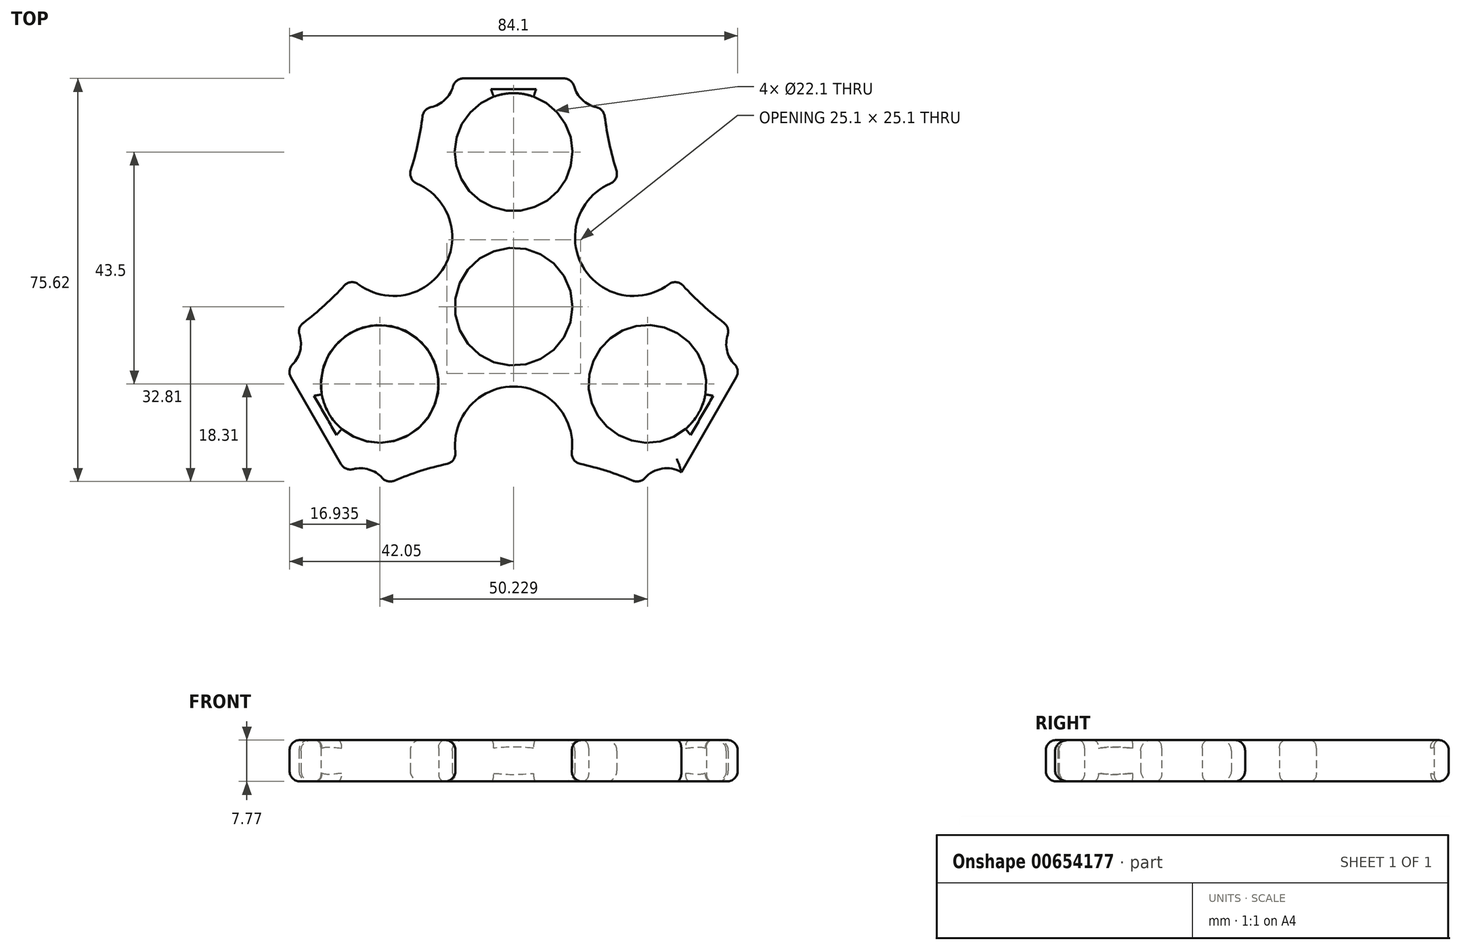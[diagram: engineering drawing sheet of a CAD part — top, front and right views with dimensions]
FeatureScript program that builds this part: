
annotation { "Feature Type Name" : "Feature", "Feature Type Description" : "" }
export const myFeature = defineFeature(function(context is Context, id is Id, definition is map)
    precondition{}
    {
        {
            var Q0;
            Q0=qCreatedBy(makeId("Top.planeOp"),FACE);
            var sketch = newSketch(context, id + "F0", { "sketchPlane" : qUnion([Q0])});
            skLineSegment(sketch, "E0", {"start": v(0, 0) * mm, "end": v(-25.11, -14.5) * mm});
            skLineSegment(sketch, "E1", {"start": v(-25.11, -14.5) * mm, "end": v(0, 0) * mm});
            skLineSegment(sketch, "E2", {"start": v(0, 0) * mm, "end": v(0, 29) * mm});
            skLineSegment(sketch, "E3", {"start": v(0, 29) * mm, "end": v(0, 0) * mm});
            skLineSegment(sketch, "E4", {"start": v(0, 0) * mm, "end": v(25.11, -14.5) * mm});
            skLineSegment(sketch, "E5", {"start": v(25.11, -14.5) * mm, "end": v(0, 0) * mm});
            skCircle(sketch, "E6", {"center": v(0, 29) * mm, "radius": 11.05 * mm});
            skCircle(sketch, "E7", {"center": v(-25.11, -14.5) * mm, "radius": 11.05 * mm});
            skCircle(sketch, "E8", {"center": v(25.11, -14.5) * mm, "radius": 11.05 * mm});
            skCircle(sketch, "E9", {"center": v(0, 0) * mm, "radius": 11.05 * mm});
            skCircle(sketch, "E10", {"center": v(-25.11, -14.5) * mm, "radius": 12.5 * mm});
            skCircle(sketch, "E11", {"center": v(0, 29) * mm, "radius": 12.5 * mm});
            skCircle(sketch, "E12", {"center": v(25.11, -14.5) * mm, "radius": 12.5 * mm});
            skLineSegment(sketch, "E13.0", {"start": v(74.15, 42.8) * mm, "end": v(0, -85.62) * mm});
            skLineSegment(sketch, "E13.1", {"start": v(0, -85.62) * mm, "end": v(-74.15, 42.8) * mm});
            skLineSegment(sketch, "E13.2", {"start": v(-74.15, 42.8) * mm, "end": v(74.15, 42.8) * mm});
            skPoint(sketch, "E13.0.midPoint", {"position": v(37.07, -21.4) * mm});
            skCircle(sketch, "E14", {"center": v(-74.15, 42.8) * mm, "radius": 57.5 * mm});
            skCircle(sketch, "E15", {"center": v(74.15, 42.8) * mm, "radius": 57.5 * mm});
            skCircle(sketch, "E16", {"center": v(0, -85.62) * mm, "radius": 57.5 * mm});
            skCircle(sketch, "E17", {"center": v(16.65, 42.8) * mm, "radius": 5.5 * mm});
            skCircle(sketch, "E18", {"center": v(-16.65, 42.8) * mm, "radius": 5.5 * mm});
            skCircle(sketch, "E19", {"center": v(-45.4, -6.99) * mm, "radius": 5.5 * mm});
            skCircle(sketch, "E20", {"center": v(-28.75, -35.82) * mm, "radius": 5.5 * mm});
            skCircle(sketch, "E21", {"center": v(28.75, -35.82) * mm, "radius": 5.5 * mm});
            skCircle(sketch, "E22", {"center": v(45.4, -6.99) * mm, "radius": 5.5 * mm});
            skLineSegment(sketch, "E23", {"start": v(25.11, -14.5) * mm, "end": v(-24.35, 14.06) * mm});
            skLineSegment(sketch, "E24", {"start": v(-25.11, -14.5) * mm, "end": v(24.35, 14.06) * mm});
            skLineSegment(sketch, "E25", {"start": v(0, 29) * mm, "end": v(0, -28.12) * mm});
            skCircle(sketch, "E26", {"center": v(22.52, 13) * mm, "radius": 11 * mm});
            skCircle(sketch, "E27", {"center": v(0, -26) * mm, "radius": 11 * mm});
            skCircle(sketch, "E28", {"center": v(-22.52, 13) * mm, "radius": 11 * mm});
            skSolve(sketch);
        }
        {
            var Q0;
            Q0=makeQuery(id+"F0.imprint","IMPRINT",FACE,{"disambiguationData":[TD([[makeQuery(id+"F0.imprint","IMPRINT",EDGE,{"derivedFrom":sQuery(id+"F0.wireOp",EDGE,"E11")}),-1.0]])]});
            var Q1;
            Q1=makeQuery(id+"F0.imprint","IMPRINT",FACE,{"disambiguationData":[TD([[makeQuery(id+"F0.imprint","IMPRINT",EDGE,{"derivedFrom":sQuery(id+"F0.wireOp",EDGE,"E10")}),-1.0]])]});
            var Q2;
            Q2=makeQuery(id+"F0.imprint","IMPRINT",FACE,{"disambiguationData":[TD([[makeQuery(id+"F0.imprint","IMPRINT",EDGE,{"derivedFrom":sQuery(id+"F0.wireOp",EDGE,"E12")}),-1.0]])]});
            var Q3;
            Q3=makeQuery(id+"F0.imprint","IMPRINT",FACE,{"disambiguationData":[TD([[makeQuery(id+"F0.imprint","IMPRINT",EDGE,{"derivedFrom":sQuery(id+"F0.wireOp",EDGE,"E6")}),-1.0]])]});
            var Q4;
            Q4=makeQuery(id+"F0.imprint","IMPRINT",FACE,{"disambiguationData":[TD([[makeQuery(id+"F0.imprint","IMPRINT",EDGE,{"derivedFrom":sQuery(id+"F0.wireOp",EDGE,"E7")}),-1.0]])]});
            var Q5;
            Q5=makeQuery(id+"F0.imprint","IMPRINT",FACE,{"disambiguationData":[TD([[makeQuery(id+"F0.imprint","IMPRINT",EDGE,{"derivedFrom":sQuery(id+"F0.wireOp",EDGE,"E8")}),-1.0]])]});
            extrude(context, id + "F1", {"entities" : qUnion([Q0, Q1, Q2, Q3, Q4, Q5]), "depth" : 7.77 * mm, "offsetDistance" : 25 * mm});
        }
        {
            var Q0;
            Q0=makeQuery(id+"F1.opExtrude","CAP_EDGE",EDGE,{"disambiguationData":[OSD([sQuery(id+"F0.wireOp",EDGE,"E13.2")])],"isStart":false});
            var Q1;
            Q1=makeQuery(id+"F1.opExtrude","CAP_EDGE",EDGE,{"disambiguationData":[OSD([sQuery(id+"F0.wireOp",EDGE,"E18")])],"isStart":true});
            var Q2;
            {var subQ0=sQuery(id+"F0.wireOp",EDGE,"E14");Q2=makeQuery(id+"F1.opExtrude","CAP_EDGE",EDGE,{"disambiguationData":[OSD([subQ0]),TDD([makeQuery(id+"F0.imprint","IMPRINT",EDGE,{"disambiguationData":[TD([[makeQuery(id+"F0.imprint","INTERSECT",VERTEX,{"disambiguationData":[OD(1.0)],"derivedFrom":[subQ0,sQuery(id+"F0.wireOp",EDGE,"tso12NrA-vn6K-p382-kDVD-uUXhCmWPkcJA")]}),-1.0]])],"derivedFrom":subQ0})])],"isStart":false});}
            var Q3;
            Q3=makeQuery(id+"F1.opExtrude","CAP_EDGE",EDGE,{"disambiguationData":[OSD([sQuery(id+"F0.wireOp",EDGE,"E18")])],"isStart":false});
            var Q4;
            Q4=makeQuery(id+"F1.opExtrude","CAP_EDGE",EDGE,{"disambiguationData":[OSD([sQuery(id+"F0.wireOp",EDGE,"tso12NrA-vn6K-p382-kDVD-uUXhCmWPkcJA")])],"isStart":false});
            var Q5;
            {var subQ0=sQuery(id+"F0.wireOp",EDGE,"E14");Q5=makeQuery(id+"F1.opExtrude","CAP_EDGE",EDGE,{"disambiguationData":[OSD([subQ0]),TDD([makeQuery(id+"F0.imprint","IMPRINT",EDGE,{"disambiguationData":[TD([[makeQuery(id+"F0.imprint","INTERSECT",VERTEX,{"disambiguationData":[OD(1.0)],"derivedFrom":[subQ0,sQuery(id+"F0.wireOp",EDGE,"E19")]}),-1.0]])],"derivedFrom":subQ0})])],"isStart":false});}
            var Q6;
            Q6=makeQuery(id+"F1.opExtrude","CAP_EDGE",EDGE,{"disambiguationData":[OSD([sQuery(id+"F0.wireOp",EDGE,"E19")])],"isStart":false});
            var Q7;
            Q7=makeQuery(id+"F1.opExtrude","CAP_EDGE",EDGE,{"disambiguationData":[OSD([sQuery(id+"F0.wireOp",EDGE,"E13.1")])],"isStart":false});
            var Q8;
            Q8=makeQuery(id+"F1.opExtrude","CAP_EDGE",EDGE,{"disambiguationData":[OSD([sQuery(id+"F0.wireOp",EDGE,"E20")])],"isStart":false});
            var Q9;
            {var subQ0=sQuery(id+"F0.wireOp",EDGE,"E16");Q9=makeQuery(id+"F1.opExtrude","CAP_EDGE",EDGE,{"disambiguationData":[OSD([subQ0]),TDD([makeQuery(id+"F0.imprint","IMPRINT",EDGE,{"disambiguationData":[TD([[makeQuery(id+"F0.imprint","INTERSECT",VERTEX,{"disambiguationData":[OD(1.0)],"derivedFrom":[subQ0,sQuery(id+"F0.wireOp",EDGE,"W5DYfLWn-jYW6-ROIx-5Qjh-cELPhGJE8ypl")]}),-1.0]])],"derivedFrom":subQ0})])],"isStart":false});}
            var Q10;
            Q10=makeQuery(id+"F1.opExtrude","CAP_EDGE",EDGE,{"disambiguationData":[OSD([sQuery(id+"F0.wireOp",EDGE,"W5DYfLWn-jYW6-ROIx-5Qjh-cELPhGJE8ypl")])],"isStart":false});
            var Q11;
            {var subQ0=sQuery(id+"F0.wireOp",EDGE,"E16");Q11=makeQuery(id+"F1.opExtrude","CAP_EDGE",EDGE,{"disambiguationData":[OSD([subQ0]),TDD([makeQuery(id+"F0.imprint","IMPRINT",EDGE,{"disambiguationData":[TD([[makeQuery(id+"F0.imprint","INTERSECT",VERTEX,{"disambiguationData":[OD(1.0)],"derivedFrom":[subQ0,sQuery(id+"F0.wireOp",EDGE,"E21")]}),-1.0]])],"derivedFrom":subQ0})])],"isStart":false});}
            var Q12;
            Q12=makeQuery(id+"F1.opExtrude","CAP_EDGE",EDGE,{"disambiguationData":[OSD([sQuery(id+"F0.wireOp",EDGE,"E21")])],"isStart":false});
            var Q13;
            Q13=makeQuery(id+"F1.opExtrude","CAP_EDGE",EDGE,{"disambiguationData":[OSD([sQuery(id+"F0.wireOp",EDGE,"E13.0")])],"isStart":false});
            var Q14;
            Q14=makeQuery(id+"F1.opExtrude","CAP_EDGE",EDGE,{"disambiguationData":[OSD([sQuery(id+"F0.wireOp",EDGE,"E22")])],"isStart":false});
            var Q15;
            {var subQ0=sQuery(id+"F0.wireOp",EDGE,"E15");Q15=makeQuery(id+"F1.opExtrude","CAP_EDGE",EDGE,{"disambiguationData":[OSD([subQ0]),TDD([makeQuery(id+"F0.imprint","IMPRINT",EDGE,{"disambiguationData":[TD([[makeQuery(id+"F0.imprint","INTERSECT",VERTEX,{"disambiguationData":[OD(1.0)],"derivedFrom":[subQ0,sQuery(id+"F0.wireOp",EDGE,"gOxveVNV-1YZB-HPbS-OaDW-XKyIJjo2ujh9")]}),-1.0]])],"derivedFrom":subQ0})])],"isStart":false});}
            var Q16;
            Q16=makeQuery(id+"F1.opExtrude","CAP_EDGE",EDGE,{"disambiguationData":[OSD([sQuery(id+"F0.wireOp",EDGE,"gOxveVNV-1YZB-HPbS-OaDW-XKyIJjo2ujh9")])],"isStart":false});
            var Q17;
            {var subQ0=sQuery(id+"F0.wireOp",EDGE,"E15");Q17=makeQuery(id+"F1.opExtrude","CAP_EDGE",EDGE,{"disambiguationData":[OSD([subQ0]),TDD([makeQuery(id+"F0.imprint","IMPRINT",EDGE,{"disambiguationData":[TD([[makeQuery(id+"F0.imprint","INTERSECT",VERTEX,{"disambiguationData":[OD(1.0)],"derivedFrom":[subQ0,sQuery(id+"F0.wireOp",EDGE,"E17")]}),-1.0]])],"derivedFrom":subQ0})])],"isStart":false});}
            var Q18;
            Q18=makeQuery(id+"F1.opExtrude","CAP_EDGE",EDGE,{"disambiguationData":[OSD([sQuery(id+"F0.wireOp",EDGE,"E17")])],"isStart":false});
            var Q19;
            Q19=makeQuery(id+"F1.opExtrude","CAP_EDGE",EDGE,{"disambiguationData":[OSD([sQuery(id+"F0.wireOp",EDGE,"E13.2")])],"isStart":true});
            var Q20;
            Q20=makeQuery(id+"F1.opExtrude","CAP_EDGE",EDGE,{"disambiguationData":[OSD([sQuery(id+"F0.wireOp",EDGE,"E17")])],"isStart":true});
            var Q21;
            {var subQ0=sQuery(id+"F0.wireOp",EDGE,"E15");Q21=makeQuery(id+"F1.opExtrude","CAP_EDGE",EDGE,{"disambiguationData":[OSD([subQ0]),TDD([makeQuery(id+"F0.imprint","IMPRINT",EDGE,{"disambiguationData":[TD([[makeQuery(id+"F0.imprint","INTERSECT",VERTEX,{"disambiguationData":[OD(1.0)],"derivedFrom":[subQ0,sQuery(id+"F0.wireOp",EDGE,"E17")]}),-1.0]])],"derivedFrom":subQ0})])],"isStart":true});}
            var Q22;
            Q22=makeQuery(id+"F1.opExtrude","CAP_EDGE",EDGE,{"disambiguationData":[OSD([sQuery(id+"F0.wireOp",EDGE,"gOxveVNV-1YZB-HPbS-OaDW-XKyIJjo2ujh9")])],"isStart":true});
            var Q23;
            {var subQ0=sQuery(id+"F0.wireOp",EDGE,"E14");Q23=makeQuery(id+"F1.opExtrude","CAP_EDGE",EDGE,{"disambiguationData":[OSD([subQ0]),TDD([makeQuery(id+"F0.imprint","IMPRINT",EDGE,{"disambiguationData":[TD([[makeQuery(id+"F0.imprint","INTERSECT",VERTEX,{"disambiguationData":[OD(1.0)],"derivedFrom":[subQ0,sQuery(id+"F0.wireOp",EDGE,"tso12NrA-vn6K-p382-kDVD-uUXhCmWPkcJA")]}),-1.0]])],"derivedFrom":subQ0})])],"isStart":true});}
            var Q24;
            Q24=makeQuery(id+"F1.opExtrude","CAP_EDGE",EDGE,{"disambiguationData":[OSD([sQuery(id+"F0.wireOp",EDGE,"tso12NrA-vn6K-p382-kDVD-uUXhCmWPkcJA")])],"isStart":true});
            var Q25;
            {var subQ0=sQuery(id+"F0.wireOp",EDGE,"E15");Q25=makeQuery(id+"F1.opExtrude","CAP_EDGE",EDGE,{"disambiguationData":[OSD([subQ0]),TDD([makeQuery(id+"F0.imprint","IMPRINT",EDGE,{"disambiguationData":[TD([[makeQuery(id+"F0.imprint","INTERSECT",VERTEX,{"disambiguationData":[OD(1.0)],"derivedFrom":[subQ0,sQuery(id+"F0.wireOp",EDGE,"gOxveVNV-1YZB-HPbS-OaDW-XKyIJjo2ujh9")]}),-1.0]])],"derivedFrom":subQ0})])],"isStart":true});}
            var Q26;
            Q26=makeQuery(id+"F1.opExtrude","CAP_EDGE",EDGE,{"disambiguationData":[OSD([sQuery(id+"F0.wireOp",EDGE,"E22")])],"isStart":true});
            var Q27;
            Q27=makeQuery(id+"F1.opExtrude","CAP_EDGE",EDGE,{"disambiguationData":[OSD([sQuery(id+"F0.wireOp",EDGE,"E13.0")])],"isStart":true});
            var Q28;
            Q28=makeQuery(id+"F1.opExtrude","CAP_EDGE",EDGE,{"disambiguationData":[OSD([sQuery(id+"F0.wireOp",EDGE,"E21")])],"isStart":true});
            var Q29;
            {var subQ0=sQuery(id+"F0.wireOp",EDGE,"E16");Q29=makeQuery(id+"F1.opExtrude","CAP_EDGE",EDGE,{"disambiguationData":[OSD([subQ0]),TDD([makeQuery(id+"F0.imprint","IMPRINT",EDGE,{"disambiguationData":[TD([[makeQuery(id+"F0.imprint","INTERSECT",VERTEX,{"disambiguationData":[OD(1.0)],"derivedFrom":[subQ0,sQuery(id+"F0.wireOp",EDGE,"E21")]}),-1.0]])],"derivedFrom":subQ0})])],"isStart":true});}
            var Q30;
            Q30=makeQuery(id+"F1.opExtrude","CAP_EDGE",EDGE,{"disambiguationData":[OSD([sQuery(id+"F0.wireOp",EDGE,"W5DYfLWn-jYW6-ROIx-5Qjh-cELPhGJE8ypl")])],"isStart":true});
            var Q31;
            {var subQ0=sQuery(id+"F0.wireOp",EDGE,"E16");Q31=makeQuery(id+"F1.opExtrude","CAP_EDGE",EDGE,{"disambiguationData":[OSD([subQ0]),TDD([makeQuery(id+"F0.imprint","IMPRINT",EDGE,{"disambiguationData":[TD([[makeQuery(id+"F0.imprint","INTERSECT",VERTEX,{"disambiguationData":[OD(1.0)],"derivedFrom":[subQ0,sQuery(id+"F0.wireOp",EDGE,"W5DYfLWn-jYW6-ROIx-5Qjh-cELPhGJE8ypl")]}),-1.0]])],"derivedFrom":subQ0})])],"isStart":true});}
            var Q32;
            Q32=makeQuery(id+"F1.opExtrude","CAP_EDGE",EDGE,{"disambiguationData":[OSD([sQuery(id+"F0.wireOp",EDGE,"E20")])],"isStart":true});
            var Q33;
            Q33=makeQuery(id+"F1.opExtrude","CAP_EDGE",EDGE,{"disambiguationData":[OSD([sQuery(id+"F0.wireOp",EDGE,"E13.1")])],"isStart":true});
            var Q34;
            Q34=makeQuery(id+"F1.opExtrude","CAP_EDGE",EDGE,{"disambiguationData":[OSD([sQuery(id+"F0.wireOp",EDGE,"E19")])],"isStart":true});
            var Q35;
            {var subQ0=sQuery(id+"F0.wireOp",EDGE,"E14");Q35=makeQuery(id+"F1.opExtrude","CAP_EDGE",EDGE,{"disambiguationData":[OSD([subQ0]),TDD([makeQuery(id+"F0.imprint","IMPRINT",EDGE,{"disambiguationData":[TD([[makeQuery(id+"F0.imprint","INTERSECT",VERTEX,{"disambiguationData":[OD(1.0)],"derivedFrom":[subQ0,sQuery(id+"F0.wireOp",EDGE,"E19")]}),-1.0]])],"derivedFrom":subQ0})])],"isStart":true});}
            var Q36;
            {var subQ0=sQuery(id+"F0.wireOp",EDGE,"W5DYfLWn-jYW6-ROIx-5Qjh-cELPhGJE8ypl");var subQ1=sQuery(id+"F0.wireOp",EDGE,"E16");Q36=makeQuery(id+"F1.opExtrude","SWEPT_EDGE",EDGE,{"disambiguationData":[OSD([subQ1,subQ0]),TDD([makeQuery(id+"F0.imprint","INTERSECT",VERTEX,{"disambiguationData":[OD(1.0)],"derivedFrom":[subQ1,subQ0]})])]});}
            var Q37;
            Q37=makeQuery(id+"F1.opExtrude","SWEPT_EDGE",EDGE,{"disambiguationData":[OSD([sQuery(id+"F0.wireOp",EDGE,"E16"),sQuery(id+"F0.wireOp",EDGE,"E20")])]});
            var Q38;
            Q38=makeQuery(id+"F1.opExtrude","SWEPT_EDGE",EDGE,{"disambiguationData":[OSD([sQuery(id+"F0.wireOp",EDGE,"E13.1"),sQuery(id+"F0.wireOp",EDGE,"E20")])]});
            var Q39;
            Q39=makeQuery(id+"F1.opExtrude","SWEPT_EDGE",EDGE,{"disambiguationData":[OSD([sQuery(id+"F0.wireOp",EDGE,"E13.1"),sQuery(id+"F0.wireOp",EDGE,"E19")])]});
            var Q40;
            Q40=makeQuery(id+"F1.opExtrude","SWEPT_EDGE",EDGE,{"disambiguationData":[OSD([sQuery(id+"F0.wireOp",EDGE,"E14"),sQuery(id+"F0.wireOp",EDGE,"E19")])]});
            var Q41;
            {var subQ0=sQuery(id+"F0.wireOp",EDGE,"tso12NrA-vn6K-p382-kDVD-uUXhCmWPkcJA");var subQ1=sQuery(id+"F0.wireOp",EDGE,"E14");Q41=makeQuery(id+"F1.opExtrude","SWEPT_EDGE",EDGE,{"disambiguationData":[OSD([subQ1,subQ0]),TDD([makeQuery(id+"F0.imprint","INTERSECT",VERTEX,{"disambiguationData":[OD(0.0)],"derivedFrom":[subQ1,subQ0]})])]});}
            var Q42;
            {var subQ0=sQuery(id+"F0.wireOp",EDGE,"tso12NrA-vn6K-p382-kDVD-uUXhCmWPkcJA");var subQ1=sQuery(id+"F0.wireOp",EDGE,"E14");Q42=makeQuery(id+"F1.opExtrude","SWEPT_EDGE",EDGE,{"disambiguationData":[OSD([subQ1,subQ0]),TDD([makeQuery(id+"F0.imprint","INTERSECT",VERTEX,{"disambiguationData":[OD(1.0)],"derivedFrom":[subQ1,subQ0]})])]});}
            var Q43;
            Q43=makeQuery(id+"F1.opExtrude","SWEPT_EDGE",EDGE,{"disambiguationData":[OSD([sQuery(id+"F0.wireOp",EDGE,"E14"),sQuery(id+"F0.wireOp",EDGE,"E18")])]});
            var Q44;
            Q44=makeQuery(id+"F1.opExtrude","SWEPT_EDGE",EDGE,{"disambiguationData":[OSD([sQuery(id+"F0.wireOp",EDGE,"E13.2"),sQuery(id+"F0.wireOp",EDGE,"E18")])]});
            var Q45;
            Q45=makeQuery(id+"F1.opExtrude","SWEPT_EDGE",EDGE,{"disambiguationData":[OSD([sQuery(id+"F0.wireOp",EDGE,"E13.2"),sQuery(id+"F0.wireOp",EDGE,"E17")])]});
            var Q46;
            Q46=makeQuery(id+"F1.opExtrude","SWEPT_EDGE",EDGE,{"disambiguationData":[OSD([sQuery(id+"F0.wireOp",EDGE,"E15"),sQuery(id+"F0.wireOp",EDGE,"E17")])]});
            var Q47;
            {var subQ0=sQuery(id+"F0.wireOp",EDGE,"gOxveVNV-1YZB-HPbS-OaDW-XKyIJjo2ujh9");var subQ1=sQuery(id+"F0.wireOp",EDGE,"E15");Q47=makeQuery(id+"F1.opExtrude","SWEPT_EDGE",EDGE,{"disambiguationData":[OSD([subQ1,subQ0]),TDD([makeQuery(id+"F0.imprint","INTERSECT",VERTEX,{"disambiguationData":[OD(0.0)],"derivedFrom":[subQ1,subQ0]})])]});}
            var Q48;
            Q48=makeQuery(id+"F1.opExtrude","SWEPT_EDGE",EDGE,{"disambiguationData":[OSD([sQuery(id+"F0.wireOp",EDGE,"E15"),sQuery(id+"F0.wireOp",EDGE,"E22")])]});
            var Q49;
            Q49=makeQuery(id+"F1.opExtrude","SWEPT_EDGE",EDGE,{"disambiguationData":[OSD([sQuery(id+"F0.wireOp",EDGE,"E13.0"),sQuery(id+"F0.wireOp",EDGE,"E22")])]});
            var Q50;
            {var subQ0=sQuery(id+"F0.wireOp",EDGE,"gOxveVNV-1YZB-HPbS-OaDW-XKyIJjo2ujh9");var subQ1=sQuery(id+"F0.wireOp",EDGE,"E15");Q50=makeQuery(id+"F1.opExtrude","SWEPT_EDGE",EDGE,{"disambiguationData":[OSD([subQ1,subQ0]),TDD([makeQuery(id+"F0.imprint","INTERSECT",VERTEX,{"disambiguationData":[OD(1.0)],"derivedFrom":[subQ1,subQ0]})])]});}
            var Q51;
            Q51=makeQuery(id+"F1.opExtrude","SWEPT_EDGE",EDGE,{"disambiguationData":[OSD([sQuery(id+"F0.wireOp",EDGE,"E16"),sQuery(id+"F0.wireOp",EDGE,"E21")])]});
            var Q52;
            Q52=makeQuery(id+"F1.opExtrude","SWEPT_FACE",FACE,{"disambiguationData":[OSD([sQuery(id+"F0.wireOp",EDGE,"W5DYfLWn-jYW6-ROIx-5Qjh-cELPhGJE8ypl")])]});
            var Q53;
            {var subQ0=sQuery(id+"F0.wireOp",EDGE,"E28");var subQ1=sQuery(id+"F0.wireOp",EDGE,"E14");Q53=makeQuery(id+"F1.opExtrude","SWEPT_EDGE",EDGE,{"disambiguationData":[OSD([subQ1,subQ0]),TDD([makeQuery(id+"F0.imprint","INTERSECT",VERTEX,{"disambiguationData":[OD(1.0)],"derivedFrom":[subQ1,subQ0]})])]});}
            var Q54;
            {var subQ0=sQuery(id+"F0.wireOp",EDGE,"E27");var subQ1=sQuery(id+"F0.wireOp",EDGE,"E16");Q54=makeQuery(id+"F1.opExtrude","SWEPT_EDGE",EDGE,{"disambiguationData":[OSD([subQ1,subQ0]),TDD([makeQuery(id+"F0.imprint","INTERSECT",VERTEX,{"disambiguationData":[OD(1.0)],"derivedFrom":[subQ1,subQ0]})])]});}
            var Q55;
            {var subQ0=sQuery(id+"F0.wireOp",EDGE,"E28");var subQ1=sQuery(id+"F0.wireOp",EDGE,"E14");Q55=makeQuery(id+"F1.opExtrude","SWEPT_EDGE",EDGE,{"disambiguationData":[OSD([subQ1,subQ0]),TDD([makeQuery(id+"F0.imprint","INTERSECT",VERTEX,{"disambiguationData":[OD(0.0)],"derivedFrom":[subQ1,subQ0]})])]});}
            var Q56;
            {var subQ0=sQuery(id+"F0.wireOp",EDGE,"E26");var subQ1=sQuery(id+"F0.wireOp",EDGE,"E15");Q56=makeQuery(id+"F1.opExtrude","SWEPT_EDGE",EDGE,{"disambiguationData":[OSD([subQ1,subQ0]),TDD([makeQuery(id+"F0.imprint","INTERSECT",VERTEX,{"disambiguationData":[OD(1.0)],"derivedFrom":[subQ1,subQ0]})])]});}
            var Q57;
            {var subQ0=sQuery(id+"F0.wireOp",EDGE,"E26");var subQ1=sQuery(id+"F0.wireOp",EDGE,"E15");Q57=makeQuery(id+"F1.opExtrude","SWEPT_EDGE",EDGE,{"disambiguationData":[OSD([subQ1,subQ0]),TDD([makeQuery(id+"F0.imprint","INTERSECT",VERTEX,{"disambiguationData":[OD(0.0)],"derivedFrom":[subQ1,subQ0]})])]});}
            var Q58;
            {var subQ0=sQuery(id+"F0.wireOp",EDGE,"E27");var subQ1=sQuery(id+"F0.wireOp",EDGE,"E16");Q58=makeQuery(id+"F1.opExtrude","SWEPT_EDGE",EDGE,{"disambiguationData":[OSD([subQ1,subQ0]),TDD([makeQuery(id+"F0.imprint","INTERSECT",VERTEX,{"disambiguationData":[OD(0.0)],"derivedFrom":[subQ1,subQ0]})])]});}
            var Q59;
            Q59=makeQuery(id+"F1.opExtrude","CAP_EDGE",EDGE,{"disambiguationData":[OSD([sQuery(id+"F0.wireOp",EDGE,"E28")])],"isStart":true});
            var Q60;
            Q60=makeQuery(id+"F1.opExtrude","CAP_EDGE",EDGE,{"disambiguationData":[OSD([sQuery(id+"F0.wireOp",EDGE,"E26")])],"isStart":true});
            var Q61;
            Q61=makeQuery(id+"F1.opExtrude","CAP_EDGE",EDGE,{"disambiguationData":[OSD([sQuery(id+"F0.wireOp",EDGE,"E27")])],"isStart":true});
            var Q62;
            Q62=makeQuery(id+"F1.opExtrude","CAP_EDGE",EDGE,{"disambiguationData":[OSD([sQuery(id+"F0.wireOp",EDGE,"E28")])],"isStart":false});
            var Q63;
            Q63=makeQuery(id+"F1.opExtrude","CAP_EDGE",EDGE,{"disambiguationData":[OSD([sQuery(id+"F0.wireOp",EDGE,"E26")])],"isStart":false});
            var Q64;
            Q64=makeQuery(id+"F1.opExtrude","CAP_EDGE",EDGE,{"disambiguationData":[OSD([sQuery(id+"F0.wireOp",EDGE,"E27")])],"isStart":false});
            var Q65;
            {var subQ0=sQuery(id+"F0.wireOp",EDGE,"E15");Q65=makeQuery(id+"F1.opExtrude","SWEPT_FACE",FACE,{"disambiguationData":[OSD([subQ0]),TDD([makeQuery(id+"F0.imprint","IMPRINT",EDGE,{"disambiguationData":[TD([[makeQuery(id+"F0.imprint","INTERSECT",VERTEX,{"disambiguationData":[OD(1.0)],"derivedFrom":[subQ0,sQuery(id+"F0.wireOp",EDGE,"E26")]}),-1.0]])],"derivedFrom":subQ0})])]});}
            var Q66;
            {var subQ0=sQuery(id+"F0.wireOp",EDGE,"E14");Q66=makeQuery(id+"F1.opExtrude","CAP_EDGE",EDGE,{"disambiguationData":[OSD([subQ0]),TDD([makeQuery(id+"F0.imprint","IMPRINT",EDGE,{"disambiguationData":[TD([[makeQuery(id+"F0.imprint","INTERSECT",VERTEX,{"disambiguationData":[OD(1.0)],"derivedFrom":[subQ0,sQuery(id+"F0.wireOp",EDGE,"E28")]}),-1.0]])],"derivedFrom":subQ0})])],"isStart":false});}
            var Q67;
            {var subQ0=sQuery(id+"F0.wireOp",EDGE,"E16");Q67=makeQuery(id+"F1.opExtrude","SWEPT_FACE",FACE,{"disambiguationData":[OSD([subQ0]),TDD([makeQuery(id+"F0.imprint","IMPRINT",EDGE,{"disambiguationData":[TD([[makeQuery(id+"F0.imprint","INTERSECT",VERTEX,{"disambiguationData":[OD(1.0)],"derivedFrom":[subQ0,sQuery(id+"F0.wireOp",EDGE,"E27")]}),-1.0]])],"derivedFrom":subQ0})])]});}
            var Q68;
            {var subQ0=sQuery(id+"F0.wireOp",EDGE,"E14");Q68=makeQuery(id+"F1.opExtrude","CAP_EDGE",EDGE,{"disambiguationData":[OSD([subQ0]),TDD([makeQuery(id+"F0.imprint","IMPRINT",EDGE,{"disambiguationData":[TD([[makeQuery(id+"F0.imprint","INTERSECT",VERTEX,{"disambiguationData":[OD(1.0)],"derivedFrom":[subQ0,sQuery(id+"F0.wireOp",EDGE,"E28")]}),-1.0]])],"derivedFrom":subQ0})])],"isStart":true});}
            fillet(context, id + "F2", {"entities" : qUnion([Q0, Q1, Q2, Q3, Q4, Q5, Q6, Q7, Q8, Q9, Q10, Q11, Q12, Q13, Q14, Q15, Q16, Q17, Q18, Q19, Q20, Q21, Q22, Q23, Q24, Q25, Q26, Q27, Q28, Q29, Q30, Q31, Q32, Q33, Q34, Q35, Q36, Q37, Q38, Q39, Q40, Q41, Q42, Q43, Q44, Q45, Q46, Q47, Q48, Q49, Q50, Q51, Q52, Q53, Q54, Q55, Q56, Q57, Q58, Q59, Q60, Q61, Q62, Q63, Q64, Q65, Q66, Q67, Q68]), "radius" : 2 * mm, "tangentPropagation" : true, "allowEdgeOverflow" : false});
        }
        {
            var Q0;
            Q0=makeQuery(id+"F1.opExtrude","CAP_EDGE",EDGE,{"disambiguationData":[OSD([sQuery(id+"F0.wireOp",EDGE,"E6")])],"isStart":true});
            var Q1;
            Q1=makeQuery(id+"F1.opExtrude","CAP_EDGE",EDGE,{"disambiguationData":[OSD([sQuery(id+"F0.wireOp",EDGE,"E6")])],"isStart":false});
            var Q2;
            Q2=makeQuery(id+"F1.opExtrude","CAP_EDGE",EDGE,{"disambiguationData":[OSD([sQuery(id+"F0.wireOp",EDGE,"E9")])],"isStart":false});
            var Q3;
            Q3=makeQuery(id+"F1.opExtrude","CAP_EDGE",EDGE,{"disambiguationData":[OSD([sQuery(id+"F0.wireOp",EDGE,"E7")])],"isStart":false});
            var Q4;
            Q4=makeQuery(id+"F1.opExtrude","CAP_EDGE",EDGE,{"disambiguationData":[OSD([sQuery(id+"F0.wireOp",EDGE,"E8")])],"isStart":false});
            var Q5;
            Q5=makeQuery(id+"F1.opExtrude","CAP_EDGE",EDGE,{"disambiguationData":[OSD([sQuery(id+"F0.wireOp",EDGE,"E8")])],"isStart":true});
            var Q6;
            Q6=makeQuery(id+"F1.opExtrude","CAP_EDGE",EDGE,{"disambiguationData":[OSD([sQuery(id+"F0.wireOp",EDGE,"E9")])],"isStart":true});
            var Q7;
            Q7=makeQuery(id+"F1.opExtrude","CAP_EDGE",EDGE,{"disambiguationData":[OSD([sQuery(id+"F0.wireOp",EDGE,"E7")])],"isStart":true});
            fillet(context, id + "F3", {"entities" : qUnion([Q0, Q1, Q2, Q3, Q4, Q5, Q6, Q7]), "radius" : 1.5 * mm, "rho" : 0.5, "crossSection" : FilletCrossSection.CONIC, "allowEdgeOverflow" : false});
        }
    });
